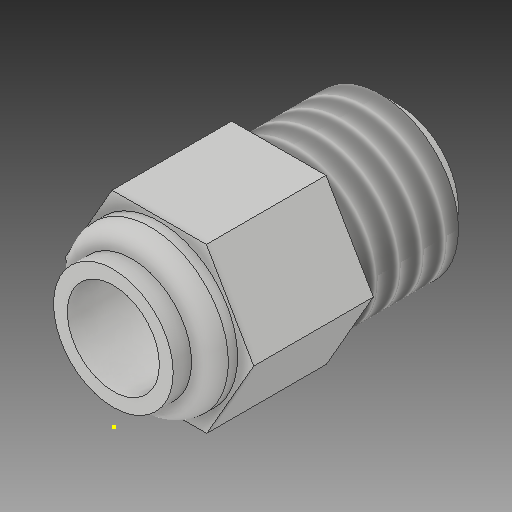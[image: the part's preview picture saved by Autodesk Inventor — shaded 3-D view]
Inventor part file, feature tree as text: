
AUTODESK INVENTOR PART (.ipt)
format: ipt  version: 2018 (Build 220112000, 112)  size: 193,024 bytes
history: native  units: mm
features: sketch x6, extrude x5, other x3, thread x1, fillet x1, chamfer x1, reference x1
ambient origin geometry x8: Origin, YZ Plane, XZ Plane, XY Plane, X Axis, Y Axis, Z Axis, Center Point
bodies: Solid1 (feature_tree)
feature tree (18):
  extrude  "Extrusion1"  Depth=10.0mm TaperAngle=0.0deg
  thread  "Thread1"  [1 undecoded]
  extrude  "Extrusion2"  Depth=1.0mm
  extrude  "Extrusion3"  Depth=1.0mm
  fillet  "Fillet1"  Radius=1.0mm
  extrude  "Extrusion4"  [1 undecoded]
  sketch  "Sketch5"
  extrude  "Extrusion5"  [1 undecoded]
  chamfer  "Chamfer1"  [1 undecoded]
  sketch  "Sketch1"  dims[d0=6.5mm d1=0.0mm d2=10.0mm d3=0.0mm d4=6.5mm d5=0.0mm]
  reference  "Reference1"
  sketch  "Sketch2"  dims[d6=1.5mm d7=0.0mm d8=1.0mm]
  sketch  "Sketch3"  dims[d9=1.0mm d10=0.0mm d11=5.0mm d12=1.0mm d13=0.0mm]
  sketch  "Sketch4"  dims[d14=1.0mm d15=2.0mm d16=45.0deg]
  sketch  "Sketch6"
  other  "<userpath>\OneDrive\Inventor\Beast 3D Printer\Hotend Mount Assembly.iam"
  other  "Hotend Mount Assembly.iam"
  other  "pshfit-mount-acrylic:1"
note: 4 required parameter values undecoded (feature->parameter linkage not recoverable at this tier; creation-order binding heuristic only, values carry confidence <= 0.55)
